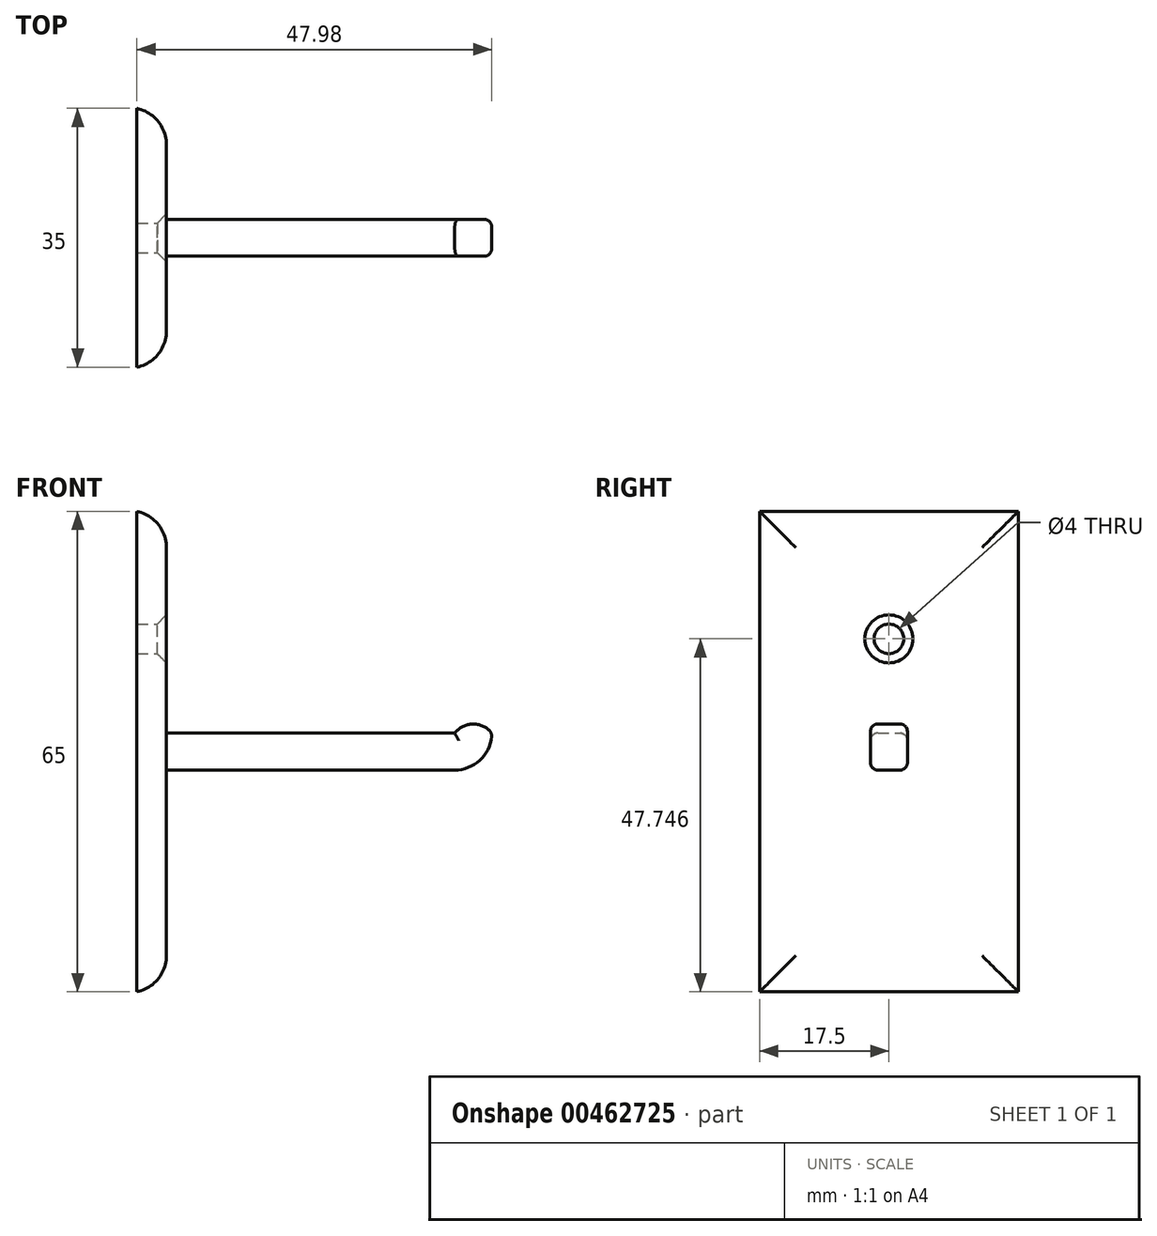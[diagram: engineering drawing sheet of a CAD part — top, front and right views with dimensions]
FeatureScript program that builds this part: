
annotation { "Feature Type Name" : "Feature", "Feature Type Description" : "" }
export const myFeature = defineFeature(function(context is Context, id is Id, definition is map)
    precondition{}
    {
        {
            var Q0;
            Q0=qCreatedBy(makeId("Front.planeOp"),FACE);
            var sketch = newSketch(context, id + "F0", { "sketchPlane" : qUnion([Q0])});
            skLineSegment(sketch, "E0", {"start": v(-13.8, 0) * mm, "end": v(25.2, 0) * mm});
            skLineSegment(sketch, "E1", {"start": v(30.2, 5) * mm, "end": v(30.2, 5) * mm});
            skLineSegment(sketch, "E2", {"start": v(30.2, 5) * mm, "end": v(-13.8, 5) * mm});
            skLineSegment(sketch, "E3", {"start": v(-13.8, 5) * mm, "end": v(-13.8, 0) * mm});
            skPoint(sketch, "E4.visualSharp", {"position": v(30.2, 0) * mm});
            skArc(sketch, "E4.filletArc", {"start": v(25.2, 0) * mm, "mid": v(28.74, 1.46) * mm, "end": v(30.2, 5) * mm});
            skArc(sketch, "E5", {"start": v(30.2, 5) * mm, "mid": v(27.7, 6.24) * mm, "end": v(25.2, 5) * mm});
            skSolve(sketch);
        }
        {
            var Q0;
            Q0 = qSketchRegion(id + "F0", true);
            extrude(context, id + "F1", {"entities" : qUnion([Q0]), "depth" : 5 * mm});
        }
        {
            var Q0;
            Q0=makeQuery(id+"F1.opExtrude","SWEPT_EDGE",EDGE,{"disambiguationData":[OSD([sQuery(id+"F0.wireOp",EDGE,"E2"),sQuery(id+"F0.wireOp",EDGE,"E4.filletArc"),sQuery(id+"F0.wireOp",EDGE,"E5")])]});
            fillet(context, id + "F2", {"entities" : qUnion([Q0]), "radius" : 1 * mm, "tangentPropagation" : true, "allowEdgeOverflow" : false});
        }
        {
            var Q0;
            Q0=makeQuery(id+"F1.opExtrude","CAP_EDGE",EDGE,{"disambiguationData":[OSD([sQuery(id+"F0.wireOp",EDGE,"E2")])],"isStart":false});
            var Q1;
            Q1=makeQuery(id+"F1.opExtrude","CAP_EDGE",EDGE,{"disambiguationData":[OSD([sQuery(id+"F0.wireOp",EDGE,"E0")])],"isStart":false});
            var Q2;
            Q2=makeQuery(id+"F1.opExtrude","CAP_EDGE",EDGE,{"disambiguationData":[OSD([sQuery(id+"F0.wireOp",EDGE,"E0")])],"isStart":true});
            var Q3;
            Q3=makeQuery(id+"F1.opExtrude","CAP_EDGE",EDGE,{"disambiguationData":[OSD([sQuery(id+"F0.wireOp",EDGE,"E2")])],"isStart":true});
            fillet(context, id + "F3", {"entities" : qUnion([Q0, Q1, Q2, Q3]), "radius" : 1 * mm, "tangentPropagation" : true, "allowEdgeOverflow" : false});
        }
        {
            var Q0;
            Q0=makeQuery(id+"F1.opExtrude","SWEPT_FACE",FACE,{"disambiguationData":[OSD([sQuery(id+"F0.wireOp",EDGE,"E3")])]});
            var sketch = newSketch(context, id + "F4", { "sketchPlane" : qUnion([Q0])});
            skLineSegment(sketch, "E6.bottom", {"start": v(20, -30) * mm, "end": v(-15, -30) * mm});
            skLineSegment(sketch, "E6.top", {"start": v(20, 35) * mm, "end": v(-15, 35) * mm});
            skLineSegment(sketch, "E6.left", {"start": v(20, -30) * mm, "end": v(20, 35) * mm});
            skLineSegment(sketch, "E6.right", {"start": v(-15, -30) * mm, "end": v(-15, 35) * mm});
            skPoint(sketch, "E6.middle", {"position": v(2.5, 2.5) * mm});
            skPoint(sketch, "E6.middle.positionSnap0", {"position": v(2.5, 0) * mm});
            skPoint(sketch, "E6.middle.positionSnap1", {"position": v(0, 2.5) * mm});
            skPoint(sketch, "E6.centerSnap0", {"position": v(2.5, 0) * mm});
            skPoint(sketch, "E6.centerSnap1", {"position": v(0, 2.5) * mm});
            skPoint(sketch, "E7.centerSnap0", {"position": v(2.5, 35) * mm});
            skSolve(sketch);
        }
        {
            var Q0;
            Q0 = qSketchRegion(id + "F4", true);
            extrude(context, id + "F5", {"entities" : qUnion([Q0]), "operationType" : NewBodyOperationType.ADD, "depth" : 4 * mm});
        }
        {
            var Q0;
            Q0=makeQuery(id+"F5.opExtrude","CAP_EDGE",EDGE,{"disambiguationData":[OSD([sQuery(id+"F4.wireOp",EDGE,"E6.left")])],"isStart":true});
            var Q1;
            Q1=makeQuery(id+"F5.opExtrude","CAP_EDGE",EDGE,{"disambiguationData":[OSD([sQuery(id+"F4.wireOp",EDGE,"E6.top")])],"isStart":true});
            var Q2;
            Q2=makeQuery(id+"F5.opExtrude","CAP_EDGE",EDGE,{"disambiguationData":[OSD([sQuery(id+"F4.wireOp",EDGE,"E6.right")])],"isStart":true});
            var Q3;
            Q3=makeQuery(id+"F5.opExtrude","CAP_EDGE",EDGE,{"disambiguationData":[OSD([sQuery(id+"F4.wireOp",EDGE,"E6.bottom")])],"isStart":true});
            var Q4;
            Q4=makeQuery(id+"F1.opExtrude","SWEPT_EDGE",EDGE,{"disambiguationData":[OSD([sQuery(id+"F0.wireOp",EDGE,"E0"),sQuery(id+"F0.wireOp",EDGE,"E3")])]});
            fillet(context, id + "F6", {"entities" : qUnion([Q0, Q1, Q2, Q3, Q4]), "radius" : 5 * mm, "tangentPropagation" : true, "allowEdgeOverflow" : false});
        }
        {
            var Q0;
            Q0=makeQuery(id+"F5.opExtrude","CAP_FACE",FACE,{"disambiguationData":[OSD([sQuery(id+"F4.wireOp",EDGE,"E6.bottom"),sQuery(id+"F4.wireOp",EDGE,"E6.top"),sQuery(id+"F4.wireOp",EDGE,"E6.left"),sQuery(id+"F4.wireOp",EDGE,"E6.right")])],"isStart":true});
            var sketch = newSketch(context, id + "F7", { "sketchPlane" : qUnion([Q0])});
            skLineSegment(sketch, "E8.0", {"start": v(10.1, 30.1) * mm, "end": v(-15.1, 30.1) * mm});
            skCircle(sketch, "E9", {"center": v(-2.5, 17.75) * mm, "radius": 2 * mm});
            skPoint(sketch, "E9.centerSnap0", {"position": v(-2.5, 30.1) * mm});
            skSolve(sketch);
        }
        {
            var Q0;
            Q0=sQuery(id+"F7.wireOp",VERTEX,"E9.center");
            var Q1;
            Q1=makeQuery(id+"F1.opExtrude","SWEPT_BODY",BODY,{"disambiguationData":[OSD([sQuery(id+"F0.wireOp",EDGE,"E0"),sQuery(id+"F0.wireOp",EDGE,"E2"),sQuery(id+"F0.wireOp",EDGE,"E3"),sQuery(id+"F0.wireOp",EDGE,"E4.filletArc"),sQuery(id+"F0.wireOp",EDGE,"E5")])]});
            hole(context, id + "F8", {"style" : HoleStyle.C_SINK, "endStyle" : HoleEndStyle.BLIND, "holeDiameter" : 4 * mm, "cSinkDiameter" : 6.5 * mm, "cSinkAngle" : 90 * degree, "holeDepth" : 4 * mm, "isTappedThrough" : true, "tappedDepth" : 12 * mm, "tapClearance" : 3, "locations" : qUnion([Q0]), "scope" : qUnion([Q1])});
        }
    });
